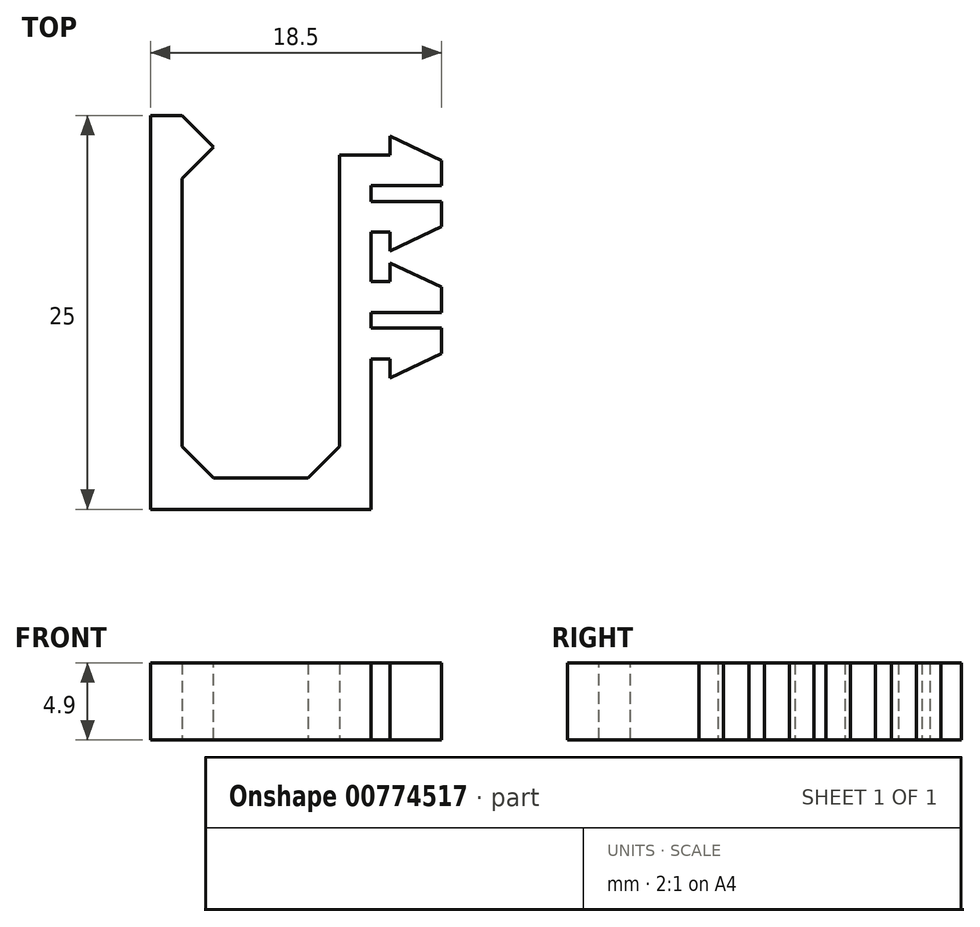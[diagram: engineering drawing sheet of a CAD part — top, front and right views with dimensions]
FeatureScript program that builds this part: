
annotation { "Feature Type Name" : "Feature", "Feature Type Description" : "" }
export const myFeature = defineFeature(function(context is Context, id is Id, definition is map)
    precondition{}
    {
        {
            var Q0;
            Q0=qCreatedBy(makeId("Top.planeOp"),FACE);
            var sketch = newSketch(context, id + "F0", { "sketchPlane" : qUnion([Q0])});
            skLineSegment(sketch, "E0", {"start": v(0, 9.55) * mm, "end": v(1.2, 9.55) * mm});
            skLineSegment(sketch, "E1", {"start": v(1.2, 9.55) * mm, "end": v(1.2, 8.35) * mm});
            skLineSegment(sketch, "E2", {"start": v(1.2, 8.35) * mm, "end": v(4.5, 9.9) * mm});
            skLineSegment(sketch, "E3", {"start": v(4.5, 11.5) * mm, "end": v(0, 11.5) * mm});
            skLineSegment(sketch, "E4", {"start": v(0, 11.5) * mm, "end": v(0, 12.5) * mm});
            skLineSegment(sketch, "E5", {"start": v(0, 12.5) * mm, "end": v(4.5, 12.5) * mm});
            skLineSegment(sketch, "E6", {"start": v(4.5, 14.1) * mm, "end": v(1.2, 15.65) * mm});
            skLineSegment(sketch, "E7", {"start": v(1.2, 15.65) * mm, "end": v(1.2, 14.45) * mm});
            skLineSegment(sketch, "E8", {"start": v(1.2, 14.45) * mm, "end": v(0, 14.45) * mm});
            skLineSegment(sketch, "E9", {"start": v(4.5, 14.1) * mm, "end": v(4.5, 12.5) * mm});
            skLineSegment(sketch, "E10", {"start": v(4.5, 11.5) * mm, "end": v(4.5, 9.9) * mm});
            skLineSegment(sketch, "E11", {"start": v(0, 17.6) * mm, "end": v(1.2, 17.6) * mm});
            skLineSegment(sketch, "E12", {"start": v(1.2, 17.6) * mm, "end": v(1.2, 16.4) * mm});
            skLineSegment(sketch, "E13", {"start": v(1.2, 16.4) * mm, "end": v(4.5, 17.95) * mm});
            skLineSegment(sketch, "E14", {"start": v(4.5, 19.55) * mm, "end": v(0, 19.55) * mm});
            skLineSegment(sketch, "E15", {"start": v(0, 19.55) * mm, "end": v(0, 20.55) * mm});
            skLineSegment(sketch, "E16", {"start": v(0, 20.55) * mm, "end": v(4.5, 20.55) * mm});
            skLineSegment(sketch, "E17", {"start": v(4.5, 22.15) * mm, "end": v(1.2, 23.7) * mm});
            skLineSegment(sketch, "E18", {"start": v(1.2, 23.7) * mm, "end": v(1.2, 22.5) * mm});
            skLineSegment(sketch, "E19", {"start": v(1.2, 22.5) * mm, "end": v(0, 22.5) * mm});
            skLineSegment(sketch, "E20", {"start": v(4.5, 22.15) * mm, "end": v(4.5, 20.55) * mm});
            skLineSegment(sketch, "E21", {"start": v(4.5, 19.55) * mm, "end": v(4.5, 17.95) * mm});
            skLineSegment(sketch, "E22", {"start": v(0, 14.45) * mm, "end": v(0, 17.6) * mm});
            skLineSegment(sketch, "E23", {"start": v(0, 9.55) * mm, "end": v(0, 0) * mm});
            skLineSegment(sketch, "E24", {"start": v(0, 0) * mm, "end": v(-14, 0) * mm});
            skLineSegment(sketch, "E25", {"start": v(-14, 0) * mm, "end": v(-14, 25) * mm});
            skLineSegment(sketch, "E26", {"start": v(0, 22.5) * mm, "end": v(-2, 22.5) * mm});
            skLineSegment(sketch, "E27", {"start": v(-2, 22.5) * mm, "end": v(-2, 2) * mm});
            skLineSegment(sketch, "E28", {"start": v(-2, 2) * mm, "end": v(-12, 2) * mm});
            skLineSegment(sketch, "E29", {"start": v(-12, 2) * mm, "end": v(-12, 21) * mm});
            skLineSegment(sketch, "E30", {"start": v(-12, 21) * mm, "end": v(-10, 23) * mm});
            skLineSegment(sketch, "E31", {"start": v(-10, 23) * mm, "end": v(-12, 25) * mm});
            skLineSegment(sketch, "E32", {"start": v(-12, 25) * mm, "end": v(-14, 25) * mm});
            skSolve(sketch);
        }
        {
            var Q0;
            Q0=makeQuery(id+"F0.imprint","IMPRINT",FACE,{"disambiguationData":[TD([[makeQuery(id+"F0.imprint","IMPRINT",EDGE,{"derivedFrom":sQuery(id+"F0.wireOp",EDGE,"E0")}),1.0]])]});
            extrude(context, id + "F1", {"entities" : qUnion([Q0]), "depth" : 4.9 * mm, "offsetDistance" : 25 * mm});
        }
        {
            var Q0;
            Q0=makeQuery(id+"F1.opExtrude","SWEPT_EDGE",EDGE,{"disambiguationData":[OSD([sQuery(id+"F0.wireOp",EDGE,"E27"),sQuery(id+"F0.wireOp",EDGE,"E28")])]});
            chamfer(context, id + "F2", {"entities" : qUnion([Q0]), "width" : 2 * mm, "tangentPropagation" : true});
        }
        {
            var Q0;
            Q0=makeQuery(id+"F1.opExtrude","SWEPT_EDGE",EDGE,{"disambiguationData":[OSD([sQuery(id+"F0.wireOp",EDGE,"E28"),sQuery(id+"F0.wireOp",EDGE,"E29")])]});
            chamfer(context, id + "F3", {"entities" : qUnion([Q0]), "width" : 2 * mm, "tangentPropagation" : true});
        }
    });
